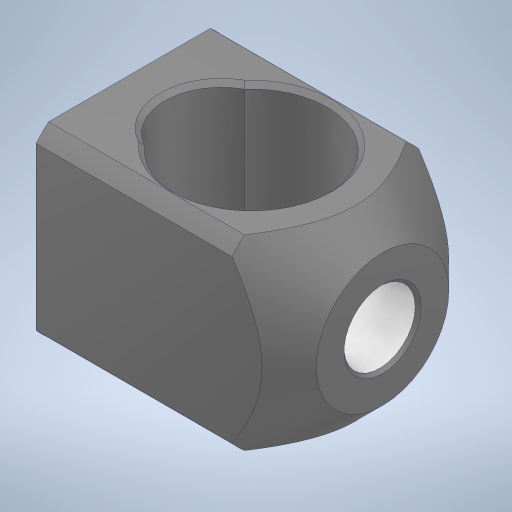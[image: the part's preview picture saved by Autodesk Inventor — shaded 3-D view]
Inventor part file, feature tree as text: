
AUTODESK INVENTOR PART (.ipt)
format: ipt  version: 2023 (Build 270158000, 158)  size: 282,624 bytes
history: mixed  units: in
note: dims shown in document units (in); Inventor stores cm internally (conversion verified against a paired STEP export)
features: extrude x1, sketch x1, other x1, imported_body x1
ambient origin geometry x8: Origin, YZ Plane, XZ Plane, XY Plane, X Axis, Y Axis, Z Axis, Center Point
bodies: Solid1 (imported_parasolid)
feature tree (4):
  extrude  "Extrusion1"  [1 undecoded]
  sketch  "Sketch1"  dims[d0=0.3937in d1=0.0in]
  other  "6669-001-1-solid1"
  imported_body  NMx_Import_Brep_tag  [imported B-rep: ~6 faces, bbox_mm=None]
note: 1 required parameter value undecoded (feature->parameter linkage not recoverable at this tier; creation-order binding heuristic only, values carry confidence <= 0.55)
